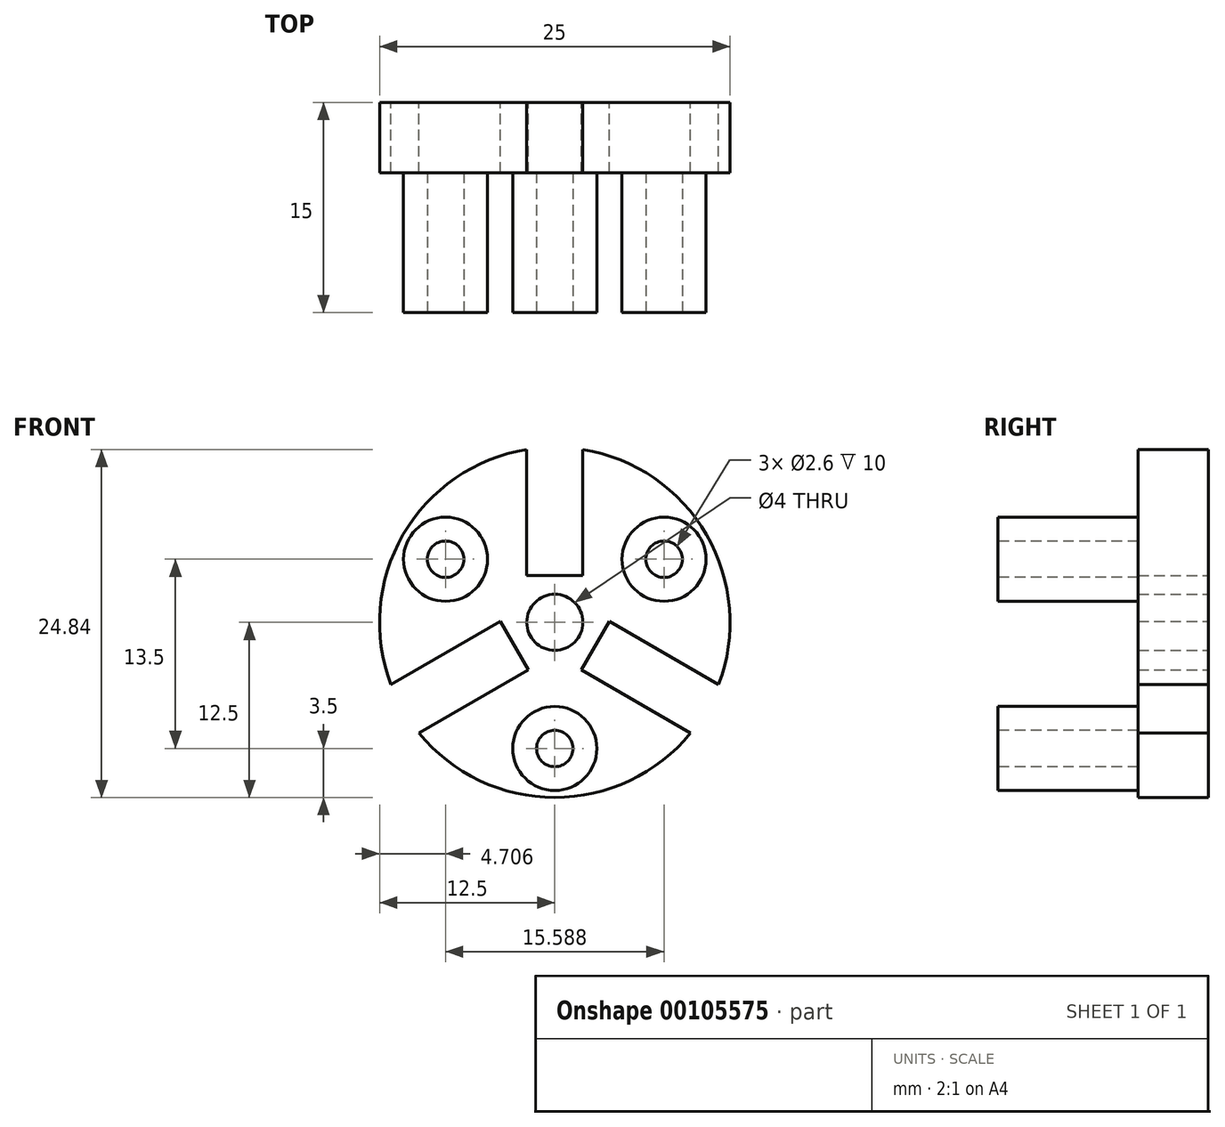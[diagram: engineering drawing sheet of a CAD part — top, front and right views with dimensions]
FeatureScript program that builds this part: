
annotation { "Feature Type Name" : "Feature", "Feature Type Description" : "" }
export const myFeature = defineFeature(function(context is Context, id is Id, definition is map)
    precondition{}
    {
        {
            var Q0;
            Q0=qCreatedBy(makeId("Front.planeOp"),FACE);
            var sketch = newSketch(context, id + "F0", { "sketchPlane" : qUnion([Q0])});
            skArc(sketch, "E0", {"start": v(-2, 12.34) * mm, "mid": v(-10.83, 6.25) * mm, "end": v(-11.69, -4.44) * mm});
            skLineSegment(sketch, "E1", {"start": v(0, 0) * mm, "end": v(0, 12.5) * mm, "construction": true});
            skLineSegment(sketch, "E2", {"start": v(0, 0) * mm, "end": v(10.83, -6.25) * mm, "construction": true});
            skLineSegment(sketch, "E3", {"start": v(0, 0) * mm, "end": v(-10.83, -6.25) * mm, "construction": true});
            skLineSegment(sketch, "E4.top", {"start": v(2, 3.34) * mm, "end": v(-2, 3.34) * mm});
            skLineSegment(sketch, "E4.left", {"start": v(2, 12.34) * mm, "end": v(2, 3.34) * mm});
            skLineSegment(sketch, "E4.right", {"start": v(-2, 12.34) * mm, "end": v(-2, 3.34) * mm});
            skPoint(sketch, "E4.middle", {"position": v(0, 7.84) * mm});
            skCircle(sketch, "E5", {"center": v(0, 0) * mm, "radius": 2 * mm});
            skLineSegment(sketch, "E6.MirrorCS", {"start": v(11.69, -4.44) * mm, "end": v(3.9, 0.06) * mm});
            skLineSegment(sketch, "E7.MirrorCS", {"start": v(9.69, -7.9) * mm, "end": v(1.9, -3.4) * mm});
            skLineSegment(sketch, "E8.MirrorCS", {"start": v(3.9, 0.06) * mm, "end": v(1.9, -3.4) * mm});
            skLineSegment(sketch, "E9.MirrorCS", {"start": v(-9.69, -7.9) * mm, "end": v(-1.9, -3.4) * mm});
            skLineSegment(sketch, "E10.MirrorCS", {"start": v(-1.9, -3.4) * mm, "end": v(-3.9, 0.06) * mm});
            skLineSegment(sketch, "E11.MirrorCS", {"start": v(-11.69, -4.44) * mm, "end": v(-3.9, 0.06) * mm});
            skArc(sketch, "E12.trimOffspring", {"start": v(11.69, -4.44) * mm, "mid": v(10.83, 6.25) * mm, "end": v(2, 12.34) * mm});
            skArc(sketch, "E13.trimOffspring", {"start": v(-9.69, -7.9) * mm, "mid": v(0, -12.5) * mm, "end": v(9.69, -7.9) * mm});
            skSolve(sketch);
        }
        {
            var Q0;
            Q0 = qSketchRegion(id + "F0", true);
            extrude(context, id + "F1", {"entities" : qUnion([Q0]), "depth" : 5 * mm});
        }
        {
            var Q0;
            Q0=makeQuery(id+"F1.opExtrude","CAP_FACE",FACE,{"disambiguationData":[OSD([sQuery(id+"F0.wireOp",EDGE,"E0"),sQuery(id+"F0.wireOp",EDGE,"E4.top"),sQuery(id+"F0.wireOp",EDGE,"E4.left"),sQuery(id+"F0.wireOp",EDGE,"E4.right"),sQuery(id+"F0.wireOp",EDGE,"E5"),sQuery(id+"F0.wireOp",EDGE,"E6.MirrorCS"),sQuery(id+"F0.wireOp",EDGE,"E7.MirrorCS"),sQuery(id+"F0.wireOp",EDGE,"E8.MirrorCS"),sQuery(id+"F0.wireOp",EDGE,"E9.MirrorCS"),sQuery(id+"F0.wireOp",EDGE,"E10.MirrorCS"),sQuery(id+"F0.wireOp",EDGE,"E11.MirrorCS"),sQuery(id+"F0.wireOp",EDGE,"E12.trimOffspring"),sQuery(id+"F0.wireOp",EDGE,"E13.trimOffspring")])],"isStart":false});
            var sketch = newSketch(context, id + "F2", { "sketchPlane" : qUnion([Q0])});
            skLineSegment(sketch, "E14", {"start": v(0, 0) * mm, "end": v(19.32, -11.15) * mm, "construction": true});
            skCircle(sketch, "E15.MirrorC", {"center": v(7.8, 4.5) * mm, "radius": 3 * mm});
            skCircle(sketch, "E16.MirrorC", {"center": v(-7.8, 4.5) * mm, "radius": 3 * mm});
            skCircle(sketch, "E17.MirrorC", {"center": v(0, -9) * mm, "radius": 3 * mm});
            skSolve(sketch);
        }
        {
            var Q0;
            Q0 = qSketchRegion(id + "F2", true);
            extrude(context, id + "F3", {"entities" : qUnion([Q0]), "operationType" : NewBodyOperationType.ADD, "depth" : 10 * mm});
        }
        {
            var Q0;
            Q0=makeQuery(id+"F3.opExtrude","CAP_FACE",FACE,{"disambiguationData":[OSD([sQuery(id+"F2.wireOp",EDGE,"E17.MirrorC")])],"isStart":false});
            var sketch = newSketch(context, id + "F4", { "sketchPlane" : qUnion([Q0])});
            skCircle(sketch, "E18", {"center": v(0, -9) * mm, "radius": 1.3 * mm});
            skLineSegment(sketch, "E19", {"start": v(0, 0) * mm, "end": v(12.82, -7.4) * mm, "construction": true});
            skCircle(sketch, "E20.MirrorC", {"center": v(7.8, 4.5) * mm, "radius": 1.3 * mm});
            skCircle(sketch, "E21.MirrorC", {"center": v(-7.8, 4.5) * mm, "radius": 1.3 * mm});
            skSolve(sketch);
        }
        {
            var Q0;
            Q0 = qSketchRegion(id + "F4", true);
            extrude(context, id + "F5", {"entities" : qUnion([Q0]), "operationType" : NewBodyOperationType.REMOVE, "oppositeDirection" : true, "depth" : 10 * mm});
        }
    });
